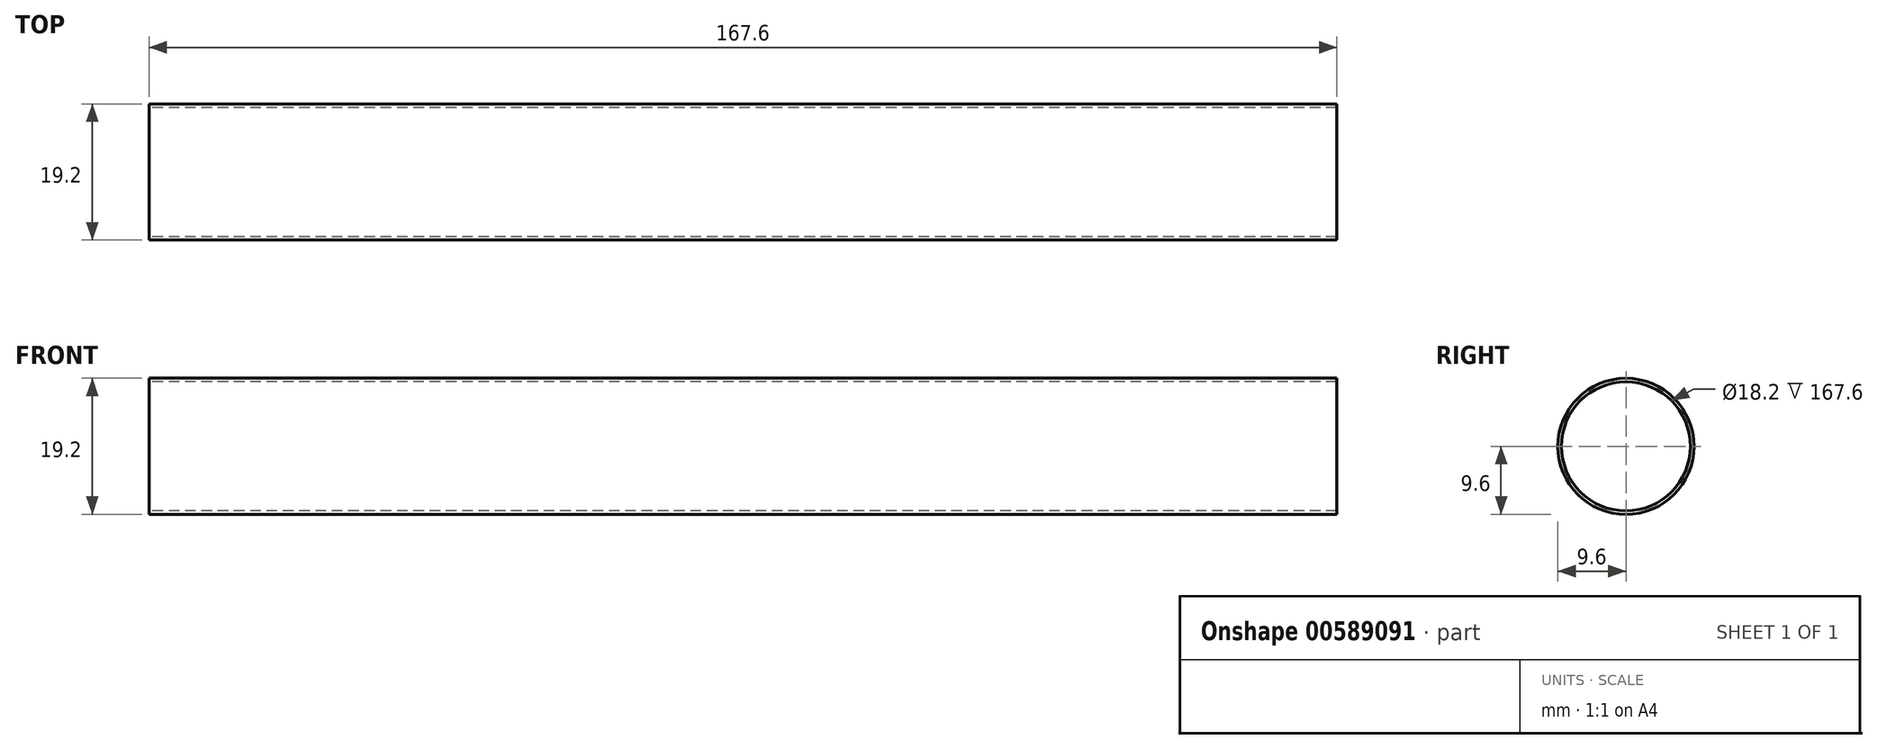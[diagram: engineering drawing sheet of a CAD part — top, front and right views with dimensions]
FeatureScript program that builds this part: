
annotation { "Feature Type Name" : "Feature", "Feature Type Description" : "" }
export const myFeature = defineFeature(function(context is Context, id is Id, definition is map)
    precondition{}
    {
        {
            var Q0;
            Q0=qCreatedBy(makeId("Front.planeOp"),FACE);
            var sketch = newSketch(context, id + "F0", { "sketchPlane" : qUnion([Q0])});
            skLineSegment(sketch, "E0", {"start": v(-83.8, 9.1) * mm, "end": v(83.8, 9.1) * mm});
            skLineSegment(sketch, "E1", {"start": v(83.8, 9.1) * mm, "end": v(83.8, 9.6) * mm});
            skLineSegment(sketch, "E2", {"start": v(83.8, 9.6) * mm, "end": v(-83.8, 9.6) * mm});
            skLineSegment(sketch, "E3", {"start": v(-83.8, 9.6) * mm, "end": v(-83.8, 9.1) * mm});
            skLineSegment(sketch, "E4", {"start": v(-83.8, 0) * mm, "end": v(83.8, 0) * mm, "construction": true});
            skSolve(sketch);
        }
        {
            var Q0;
            Q0 = qSketchRegion(id + "F0", true);
            var Q1;
            Q1=sQuery(id+"F0.wireOp",EDGE,"E4");
            revolve(context, id + "F1", {"entities" : qUnion([Q0]), "axis" : qUnion([Q1]), "revolveType" : RevolveType.FULL});
        }
    });
